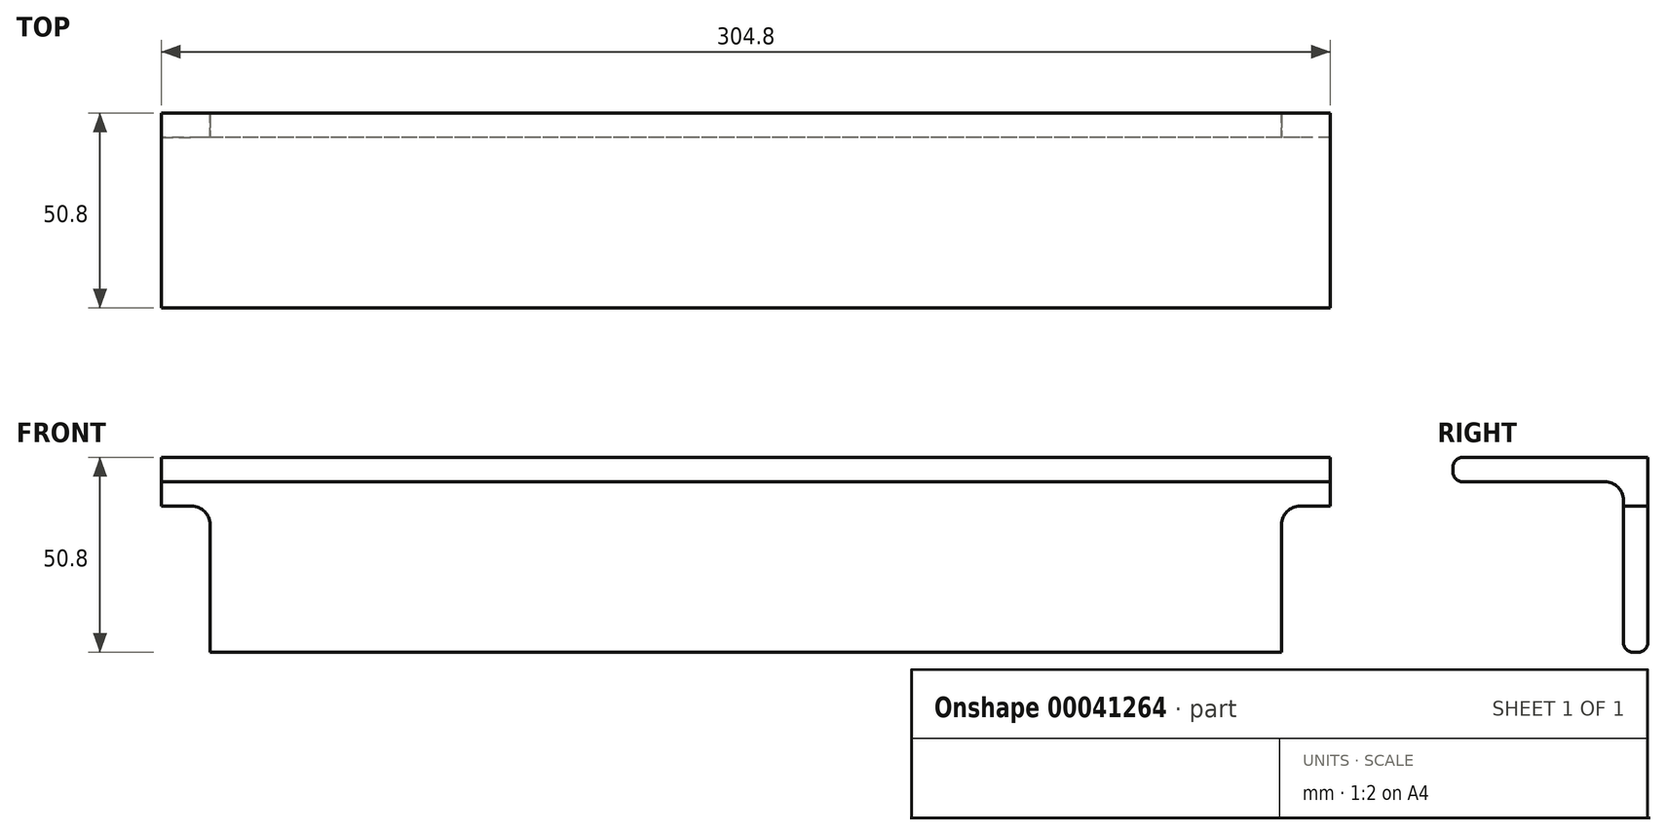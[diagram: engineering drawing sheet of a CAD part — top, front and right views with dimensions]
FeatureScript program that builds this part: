
annotation { "Feature Type Name" : "Feature", "Feature Type Description" : "" }
export const myFeature = defineFeature(function(context is Context, id is Id, definition is map)
    precondition{}
    {
        {
            var Q0;
            Q0=qCreatedBy(makeId("Right.planeOp"),FACE);
            var sketch = newSketch(context, id + "F0", { "sketchPlane" : qUnion([Q0])});
            skLineSegment(sketch, "E0", {"start": v(-22.61, 36.8) * mm, "end": v(28.19, 36.8) * mm});
            skLineSegment(sketch, "E1", {"start": v(28.19, 36.8) * mm, "end": v(28.19, -14) * mm});
            skLineSegment(sketch, "E2", {"start": v(28.19, -14) * mm, "end": v(21.84, -14) * mm});
            skLineSegment(sketch, "E3", {"start": v(21.84, -14) * mm, "end": v(21.84, 30.45) * mm});
            skLineSegment(sketch, "E4", {"start": v(21.84, 30.45) * mm, "end": v(-22.61, 30.45) * mm});
            skLineSegment(sketch, "E5", {"start": v(-22.61, 30.45) * mm, "end": v(-22.61, 36.8) * mm});
            skSolve(sketch);
        }
        {
            var Q0;
            Q0=makeQuery(id+"F0.imprint","IMPRINT",FACE,{"disambiguationData":[TD([[makeQuery(id+"F0.imprint","IMPRINT",EDGE,{"derivedFrom":sQuery(id+"F0.wireOp",EDGE,"E0")}),-1.0]])]});
            extrude(context, id + "F1", {"entities" : qUnion([Q0]), "depth" : 304.8 * mm});
        }
        {
            var Q0;
            Q0=makeQuery(id+"F1.opExtrude","SWEPT_FACE",FACE,{"disambiguationData":[OSD([sQuery(id+"F0.wireOp",EDGE,"E3")])]});
            var sketch = newSketch(context, id + "F2", { "sketchPlane" : qUnion([Q0])});
            skLineSegment(sketch, "E6.bottom", {"start": v(0, -14) * mm, "end": v(12.7, -14) * mm});
            skLineSegment(sketch, "E6.top", {"start": v(0, 24.1) * mm, "end": v(12.7, 24.1) * mm});
            skLineSegment(sketch, "E6.left", {"start": v(0, -14) * mm, "end": v(0, 24.1) * mm});
            skLineSegment(sketch, "E6.right", {"start": v(12.7, -14) * mm, "end": v(12.7, 24.1) * mm});
            skSolve(sketch);
        }
        {
            var Q0;
            Q0=makeQuery(id+"F2.imprint","IMPRINT",FACE,{"disambiguationData":[TD([[makeQuery(id+"F2.imprint","IMPRINT",EDGE,{"derivedFrom":sQuery(id+"F2.wireOp",EDGE,"E6.bottom")}),-1.0]])]});
            extrude(context, id + "F3", {"entities" : qUnion([Q0]), "operationType" : NewBodyOperationType.REMOVE, "oppositeDirection" : true, "depth" : 25.4 * mm});
        }
        {
            var Q0;
            Q0=makeQuery(id+"F1.opExtrude","SWEPT_FACE",FACE,{"disambiguationData":[OSD([sQuery(id+"F0.wireOp",EDGE,"E3")])]});
            var sketch = newSketch(context, id + "F4", { "sketchPlane" : qUnion([Q0])});
            skLineSegment(sketch, "E7.bottom", {"start": v(304.8, -14) * mm, "end": v(292.1, -14) * mm});
            skLineSegment(sketch, "E7.top", {"start": v(304.8, 24.1) * mm, "end": v(292.1, 24.1) * mm});
            skLineSegment(sketch, "E7.left", {"start": v(304.8, -14) * mm, "end": v(304.8, 24.1) * mm});
            skLineSegment(sketch, "E7.right", {"start": v(292.1, -14) * mm, "end": v(292.1, 24.1) * mm});
            skSolve(sketch);
        }
        {
            var Q0;
            Q0 = qSketchRegion(id + "F4", true);
            extrude(context, id + "F5", {"entities" : qUnion([Q0]), "operationType" : NewBodyOperationType.REMOVE, "oppositeDirection" : true, "depth" : 25.4 * mm});
        }
        {
            var Q0;
            Q0=makeQuery(id+"F1.opExtrude","SWEPT_EDGE",EDGE,{"disambiguationData":[OSD([sQuery(id+"F0.wireOp",EDGE,"E3"),sQuery(id+"F0.wireOp",EDGE,"E4")])]});
            fillet(context, id + "F6", {"entities" : qUnion([Q0]), "radius" : 4.76 * mm, "tangentPropagation" : true, "allowEdgeOverflow" : false});
        }
        {
            var Q0;
            Q0=makeQuery(id+"F1.opExtrude","SWEPT_EDGE",EDGE,{"disambiguationData":[OSD([sQuery(id+"F0.wireOp",EDGE,"E0"),sQuery(id+"F0.wireOp",EDGE,"E5")])]});
            var Q1;
            Q1=makeQuery(id+"F1.opExtrude","SWEPT_EDGE",EDGE,{"disambiguationData":[OSD([sQuery(id+"F0.wireOp",EDGE,"E4"),sQuery(id+"F0.wireOp",EDGE,"E5")])]});
            var Q2;
            Q2=makeQuery(id+"F1.opExtrude","SWEPT_EDGE",EDGE,{"disambiguationData":[OSD([sQuery(id+"F0.wireOp",EDGE,"E2"),sQuery(id+"F0.wireOp",EDGE,"E3")])]});
            var Q3;
            Q3=makeQuery(id+"F1.opExtrude","SWEPT_EDGE",EDGE,{"disambiguationData":[OSD([sQuery(id+"F0.wireOp",EDGE,"E1"),sQuery(id+"F0.wireOp",EDGE,"E2")])]});
            fillet(context, id + "F7", {"entities" : qUnion([Q0, Q1, Q2, Q3]), "radius" : 2.54 * mm, "tangentPropagation" : true, "allowEdgeOverflow" : false});
        }
        {
            var Q0;
            Q0=makeQuery(id+"F5.boolean.opBoolean","COPY",EDGE,{"derivedFrom":makeQuery(id+"F5.opExtrude","SWEPT_EDGE",EDGE,{"disambiguationData":[OSD([sQuery(id+"F4.wireOp",EDGE,"E7.top"),sQuery(id+"F4.wireOp",EDGE,"E7.right")])]})});
            var Q1;
            Q1=makeQuery(id+"F3.boolean.opBoolean","COPY",EDGE,{"derivedFrom":makeQuery(id+"F3.opExtrude","SWEPT_EDGE",EDGE,{"disambiguationData":[OSD([sQuery(id+"F2.wireOp",EDGE,"E6.top"),sQuery(id+"F2.wireOp",EDGE,"E6.right")])]})});
            fillet(context, id + "F8", {"entities" : qUnion([Q0, Q1]), "radius" : 4.76 * mm, "tangentPropagation" : true, "allowEdgeOverflow" : false});
        }
    });
